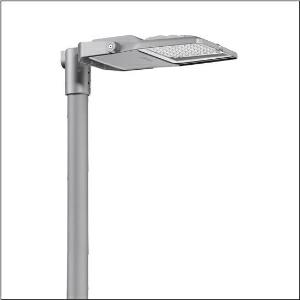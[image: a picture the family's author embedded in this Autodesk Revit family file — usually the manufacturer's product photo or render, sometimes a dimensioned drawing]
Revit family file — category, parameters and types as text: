
# Revit family: floodlight_fl_21_iq_mini___pl33t_5xa7772b2f3a_3cf2
name_source: partatom
category: Lighting Fixtures
units: mm (PartAtom-declared; Revit-internal decimal feet)

## family parameters
Cut with Voids When Loaded = No
Host = Face
Light Source = No
Part Type = Normal
Room Calculation Point = No
Round Connector Dimension = Use Diameter
Shared = No

## types (1)
- --- (1 x LED, 6170 lm, 45.5 W, 3000K)
    Apparent Load = 46 VA
    CIE Flux Codes = 26 75 99 100 100
    Color Rendering = 70
    Color Temperature = 3000K
    Default Elevation = 1800 mm
    Description = Floodlight FL 21 iQ mini, floodlight, primary light control with lens, of PMMA, primary optical cover: protective disc, of toughened safety glass, transparent, light distribution: PL33T, light emission: direct distribution, installation type: surface-mounted, LED, High Power LED, rated luminous flux: 6.170lm, luminous efficacy: 136lm/W, light colour: 730, colour temperature: 3000K, control: Auto-Match, Temp-Guard, Night-Set, Smart-Wire, Desk-Remote (wireless, voltage-free reading and setting of iQ features in the workshop via application-optimized NFC function/RFID function), optimised constant luminous flux control (CLO 2.0), Light-Fading, Lumen-Switch, with terminal, 6-pole, mains connection: 220..240V, AC, 50/60Hz, start of lifetime: 46W, end of service life: 48W, reduction: 22W, luminaire housing, of diecast aluminium, powder-coated, Siteco® metallic grey (DB 702S), corrosivity category C5 mid according to DIN EN ISO 12944, sealing non-destructively replaceable, please order mast flange separately, mast bracket, of steel, galvanised, powder-coated, protection rating (complete): IP66, insulation class (complete): insulation class II (safety insulation), certification: CE, ENEC, VDE, protection symbol: D, impact resistance: IK08, permissible operating ambient temperature: -40..+40°C, permissible operating ambient temperature for outdoor applications: -40..+50°C, standard: DIN EN 12944, LABS conformity tested according to VDMA 24364:2018-05, packaging unit: 1 piece

Light Distribution: PL33T
    Height = 70 mm
    Lamp = 1 x LED
    Lamp Light Flux = 6170 lm
    Lamp Power = 45.5 W
    Lamp count = 1
    Length = 485 mm
    Luminous efficacy = 136 lm/W
    Manufacturer = Siteco
    ModVariant = No
    Model = 5XA7772B2F3A
    Number of Poles = 1
    OnlyDefault = Yes
    Power Factor = 1
    Product Name = Floodlight FL 21 iQ mini | PL33T
    Product group = floodlight | pylon annexe
    ProductGroupID = 6200
    Protection Class = Protection class II
    Protection Degree = IP 66
    RLX_Detail_Level = 1
    RLX_Emergency_Light_Flux = 0 lm
    RLX_Emergency_Type = 0
    RLX_Emergency_Type_DB = No
    RlxData = <blob elided: 101137 chars, md5=7785e7f5>
    Socket = socket
    Standby Power = 0 W
    System Light Flux = 6170 lm
    System Power = 46 W
    Type Comments = factory setting: luminous flux: 100 % | dim-lin: 254 | 463 mA
    Type Image = l_1007125.jpg
    URL = http://relux.com
    VarID = @adj_120365
    Voltage = 0 V
    Weight = 0.00 kg
    Width = 337 mm

## geometry (parser evidence)
native form markers: Blend x4, Sweep x12
no freeform markers — native parametric forms only
